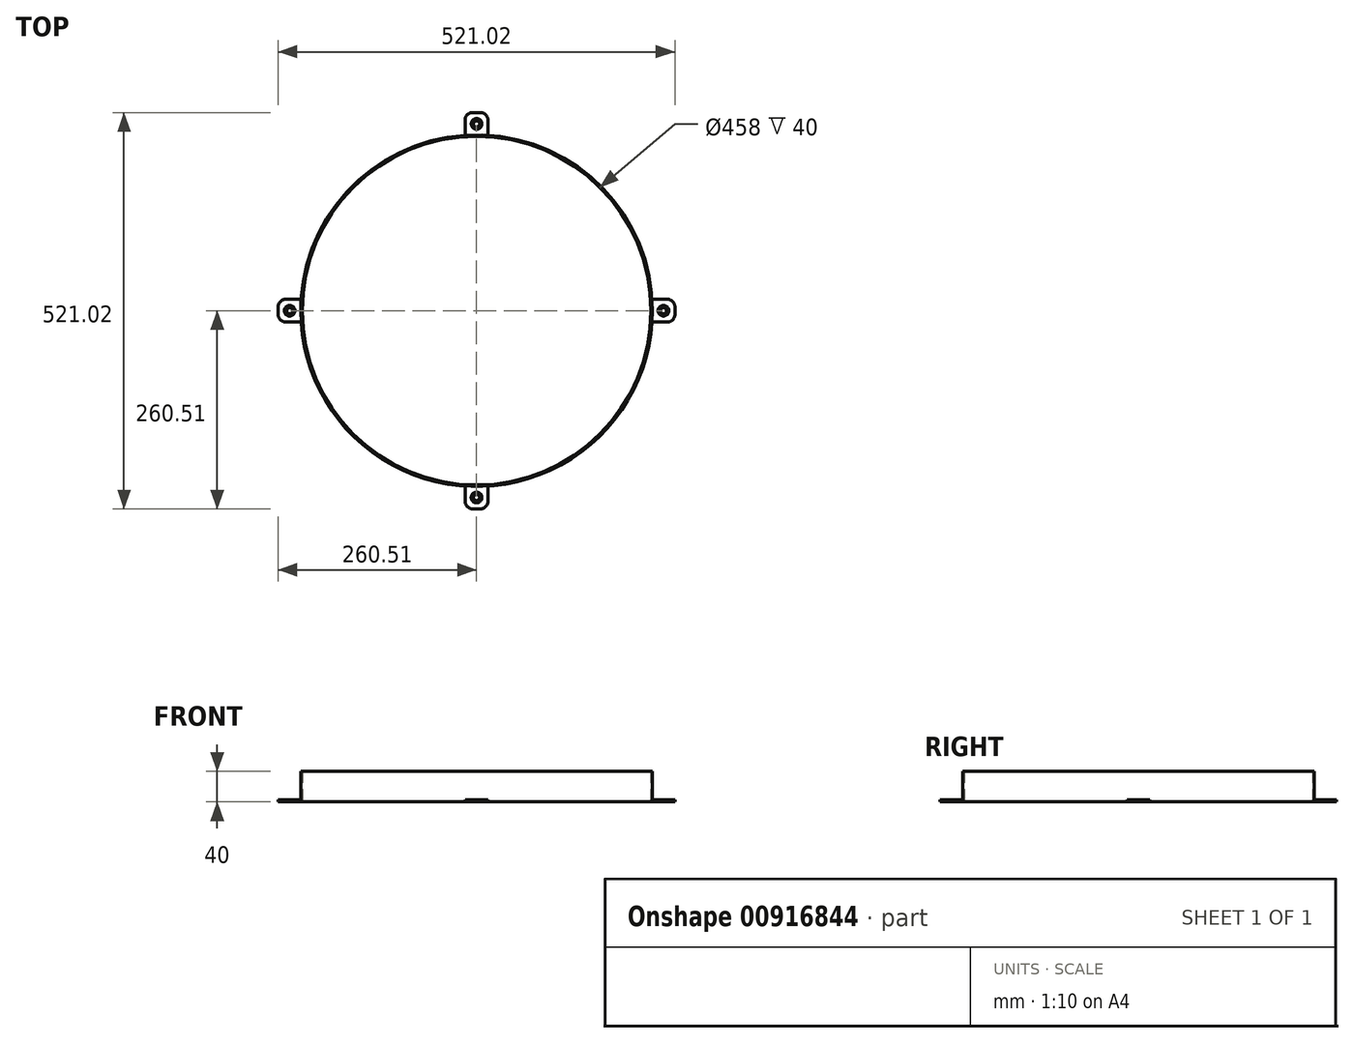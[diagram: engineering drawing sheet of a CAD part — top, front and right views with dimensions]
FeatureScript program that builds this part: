
annotation { "Feature Type Name" : "Feature", "Feature Type Description" : "" }
export const myFeature = defineFeature(function(context is Context, id is Id, definition is map)
    precondition{}
    {
        {
            var Q0;
            Q0=qCreatedBy(makeId("Top.planeOp"),FACE);
            var sketch = newSketch(context, id + "F0", { "sketchPlane" : qUnion([Q0])});
            skCircle(sketch, "E0", {"center": v(0, 0) * mm, "radius": 231 * mm});
            skCircle(sketch, "E1", {"center": v(0, 0) * mm, "radius": 229 * mm});
            skSolve(sketch);
        }
        {
            var Q0;
            Q0=qSketchRegion(id+"F0",true);
            extrude(context, id + "F1", {"entities" : qUnion([Q0]), "depth" : 40 * mm, "offsetDistance" : 25 * mm});
        }
        {
            var Q0;
            {var subQ0=makeQuery(id+"FOfs6LXXoXaqfb5_1.boolean.opBoolean","MERGE",FACE,{"derivedFrom":[makeQuery(id+"F1.opExtrude","CAP_FACE",FACE,{"disambiguationData":[OSD([sQuery(id+"F0.wireOp",EDGE,"E0"),sQuery(id+"F0.wireOp",EDGE,"E1")])],"isStart":true}),makeQuery(id+"FOfs6LXXoXaqfb5_1.opExtrude","CAP_FACE",FACE,{"disambiguationData":[OSD([sQuery(id+"Fq126zPfvdtfzcJ_1.wireOp",EDGE,"aM8YIA2p-sepS-RrJB-uuBs-LwZfDOID8hhf.bottom"),sQuery(id+"Fq126zPfvdtfzcJ_1.wireOp",EDGE,"aM8YIA2p-sepS-RrJB-uuBs-LwZfDOID8hhf.top"),sQuery(id+"Fq126zPfvdtfzcJ_1.wireOp",EDGE,"aM8YIA2p-sepS-RrJB-uuBs-LwZfDOID8hhf.left"),sQuery(id+"Fq126zPfvdtfzcJ_1.wireOp",EDGE,"HM3TmMY7-uQYK-AxsU-DERO-EDIUWc1xLfHu")])],"isStart":false})]});Q0=makeQuery(id+"F8.boolean.opBoolean","MERGE",FACE,{"derivedFrom":[subQ0,makeQuery(id+"F8.opPattern","COPY",FACE,{"derivedFrom":subQ0,"instanceName":"1"}),makeQuery(id+"F8.opPattern","COPY",FACE,{"derivedFrom":subQ0,"instanceName":"2"}),makeQuery(id+"F8.opPattern","COPY",FACE,{"derivedFrom":subQ0,"instanceName":"3"}),makeQuery(id+"F8.opPattern","COPY",FACE,{"derivedFrom":subQ0,"instanceName":"4"}),makeQuery(id+"F8.opPattern","COPY",FACE,{"derivedFrom":subQ0,"instanceName":"5"})]});}
            var sketch = newSketch(context, id + "F2", { "sketchPlane" : qUnion([Q0])});
            skLineSegment(sketch, "E2.bottom", {"start": v(-15, -230.51) * mm, "end": v(15, -230.51) * mm});
            skLineSegment(sketch, "E2.top", {"start": v(-15, -260.51) * mm, "end": v(15, -260.51) * mm});
            skLineSegment(sketch, "E2.left", {"start": v(-15, -230.51) * mm, "end": v(-15, -260.51) * mm});
            skLineSegment(sketch, "E2.right", {"start": v(15, -230.51) * mm, "end": v(15, -260.51) * mm});
            skSolve(sketch);
        }
        {
            var Q0;
            Q0=qSketchRegion(id+"F2",true);
            extrude(context, id + "F3", {"entities" : qUnion([Q0]), "operationType" : NewBodyOperationType.ADD, "oppositeDirection" : true, "depth" : 3 * mm, "offsetDistance" : 25 * mm});
        }
        {
            var Q0;
            {var subQ0=makeQuery(id+"F3.boolean.opBoolean","MERGE",FACE,{"derivedFrom":[makeQuery(id+"F1.opExtrude","CAP_FACE",FACE,{"disambiguationData":[OSD([sQuery(id+"F0.wireOp",EDGE,"E0"),sQuery(id+"F0.wireOp",EDGE,"E1")])],"isStart":true}),makeQuery(id+"F3.opExtrude","CAP_FACE",FACE,{"disambiguationData":[OSD([sQuery(id+"F2.wireOp",EDGE,"E2.bottom"),sQuery(id+"F2.wireOp",EDGE,"E2.top"),sQuery(id+"F2.wireOp",EDGE,"E2.left"),sQuery(id+"F2.wireOp",EDGE,"E2.right")])],"isStart":true})]});Q0=makeQuery(id+"F8.boolean.opBoolean","MERGE",FACE,{"derivedFrom":[subQ0,makeQuery(id+"F8.opPattern","COPY",FACE,{"derivedFrom":subQ0,"instanceName":"1"}),makeQuery(id+"F8.opPattern","COPY",FACE,{"derivedFrom":subQ0,"instanceName":"2"}),makeQuery(id+"F8.opPattern","COPY",FACE,{"derivedFrom":subQ0,"instanceName":"3"}),makeQuery(id+"F8.opPattern","COPY",FACE,{"derivedFrom":subQ0,"instanceName":"4"}),makeQuery(id+"F8.opPattern","COPY",FACE,{"derivedFrom":subQ0,"instanceName":"5"})]});}
            var sketch = newSketch(context, id + "F4", { "sketchPlane" : qUnion([Q0])});
            skCircle(sketch, "E3", {"center": v(0, -245.51) * mm, "radius": 4 * mm});
            skPoint(sketch, "E3.centerSnap0", {"position": v(0, -260.51) * mm});
            skPoint(sketch, "E3.centerSnap1", {"position": v(-15, -245.51) * mm});
            skSolve(sketch);
        }
        {
            var Q0;
            Q0=qSketchRegion(id+"F4",true);
            extrude(context, id + "F5", {"entities" : qUnion([Q0]), "operationType" : NewBodyOperationType.REMOVE, "oppositeDirection" : true, "depth" : 25 * mm, "offsetDistance" : 25 * mm});
        }
        {
            var Q0;
            Q0=makeQuery(id+"F3.opExtrude","SWEPT_EDGE",EDGE,{"disambiguationData":[OSD([sQuery(id+"F2.wireOp",EDGE,"E2.top"),sQuery(id+"F2.wireOp",EDGE,"E2.left")])]});
            var Q1;
            Q1=makeQuery(id+"F3.opExtrude","SWEPT_EDGE",EDGE,{"disambiguationData":[OSD([sQuery(id+"F2.wireOp",EDGE,"E2.top"),sQuery(id+"F2.wireOp",EDGE,"E2.right")])]});
            fillet(context, id + "F6", {"entities" : qUnion([Q0, Q1]), "radius" : 10 * mm, "tangentPropagation" : true, "allowEdgeOverflow" : false});
        }
        {
            var Q0;
            Q0=qCreatedBy(makeId("Right.planeOp"),FACE);
            var sketch = newSketch(context, id + "F7", { "sketchPlane" : qUnion([Q0])});
            skLineSegment(sketch, "E4", {"start": v(0, 0) * mm, "end": v(0, -102.23) * mm});
            skSolve(sketch);
        }
        {
            var Q0;
            Q0=makeQuery(id+"F1.opExtrude","SWEPT_BODY",BODY,{"disambiguationData":[OSD([sQuery(id+"F0.wireOp",EDGE,"E0"),sQuery(id+"F0.wireOp",EDGE,"E1")])]});
            var Q1;
            Q1=sQuery(id+"F7.wireOp",EDGE,"E4");
            circularPattern(context, id + "F8", {"operationType" : NewBodyOperationType.ADD, "entities" : qUnion([Q0]), "axis" : qUnion([Q1]), "angle" : 360 * degree, "instanceCount" : 4, "equalSpace" : true});
        }
        {
            var Q0;
            Q0=makeQuery(id+"F8.opPattern","COPY",EDGE,{"derivedFrom":makeQuery(id+"F5.boolean.opBoolean","INTERSECT",EDGE,{"derivedFrom":[makeQuery(id+"F3.opExtrude","CAP_FACE",FACE,{"disambiguationData":[OSD([sQuery(id+"F2.wireOp",EDGE,"E2.bottom"),sQuery(id+"F2.wireOp",EDGE,"E2.top"),sQuery(id+"F2.wireOp",EDGE,"E2.left"),sQuery(id+"F2.wireOp",EDGE,"E2.right")])],"isStart":false}),makeQuery(id+"F5.opExtrude","SWEPT_FACE",FACE,{"disambiguationData":[OSD([sQuery(id+"F4.wireOp",EDGE,"E3")])]})]}),"instanceName":"3"});
            var Q1;
            Q1=makeQuery(id+"F5.boolean.opBoolean","INTERSECT",EDGE,{"derivedFrom":[makeQuery(id+"F3.opExtrude","CAP_FACE",FACE,{"disambiguationData":[OSD([sQuery(id+"F2.wireOp",EDGE,"E2.bottom"),sQuery(id+"F2.wireOp",EDGE,"E2.top"),sQuery(id+"F2.wireOp",EDGE,"E2.left"),sQuery(id+"F2.wireOp",EDGE,"E2.right")])],"isStart":false}),makeQuery(id+"F5.opExtrude","SWEPT_FACE",FACE,{"disambiguationData":[OSD([sQuery(id+"F4.wireOp",EDGE,"E3")])]})]});
            var Q2;
            Q2=makeQuery(id+"F8.opPattern","COPY",EDGE,{"derivedFrom":makeQuery(id+"F5.boolean.opBoolean","INTERSECT",EDGE,{"derivedFrom":[makeQuery(id+"F3.opExtrude","CAP_FACE",FACE,{"disambiguationData":[OSD([sQuery(id+"F2.wireOp",EDGE,"E2.bottom"),sQuery(id+"F2.wireOp",EDGE,"E2.top"),sQuery(id+"F2.wireOp",EDGE,"E2.left"),sQuery(id+"F2.wireOp",EDGE,"E2.right")])],"isStart":false}),makeQuery(id+"F5.opExtrude","SWEPT_FACE",FACE,{"disambiguationData":[OSD([sQuery(id+"F4.wireOp",EDGE,"E3")])]})]}),"instanceName":"1"});
            var Q3;
            Q3=makeQuery(id+"F8.opPattern","COPY",EDGE,{"derivedFrom":makeQuery(id+"F5.boolean.opBoolean","INTERSECT",EDGE,{"derivedFrom":[makeQuery(id+"F3.opExtrude","CAP_FACE",FACE,{"disambiguationData":[OSD([sQuery(id+"F2.wireOp",EDGE,"E2.bottom"),sQuery(id+"F2.wireOp",EDGE,"E2.top"),sQuery(id+"F2.wireOp",EDGE,"E2.left"),sQuery(id+"F2.wireOp",EDGE,"E2.right")])],"isStart":false}),makeQuery(id+"F5.opExtrude","SWEPT_FACE",FACE,{"disambiguationData":[OSD([sQuery(id+"F4.wireOp",EDGE,"E3")])]})]}),"instanceName":"2"});
            chamfer(context, id + "F9", {"entities" : qUnion([Q0, Q1, Q2, Q3]), "width" : 3 * mm, "tangentPropagation" : true});
        }
    });
